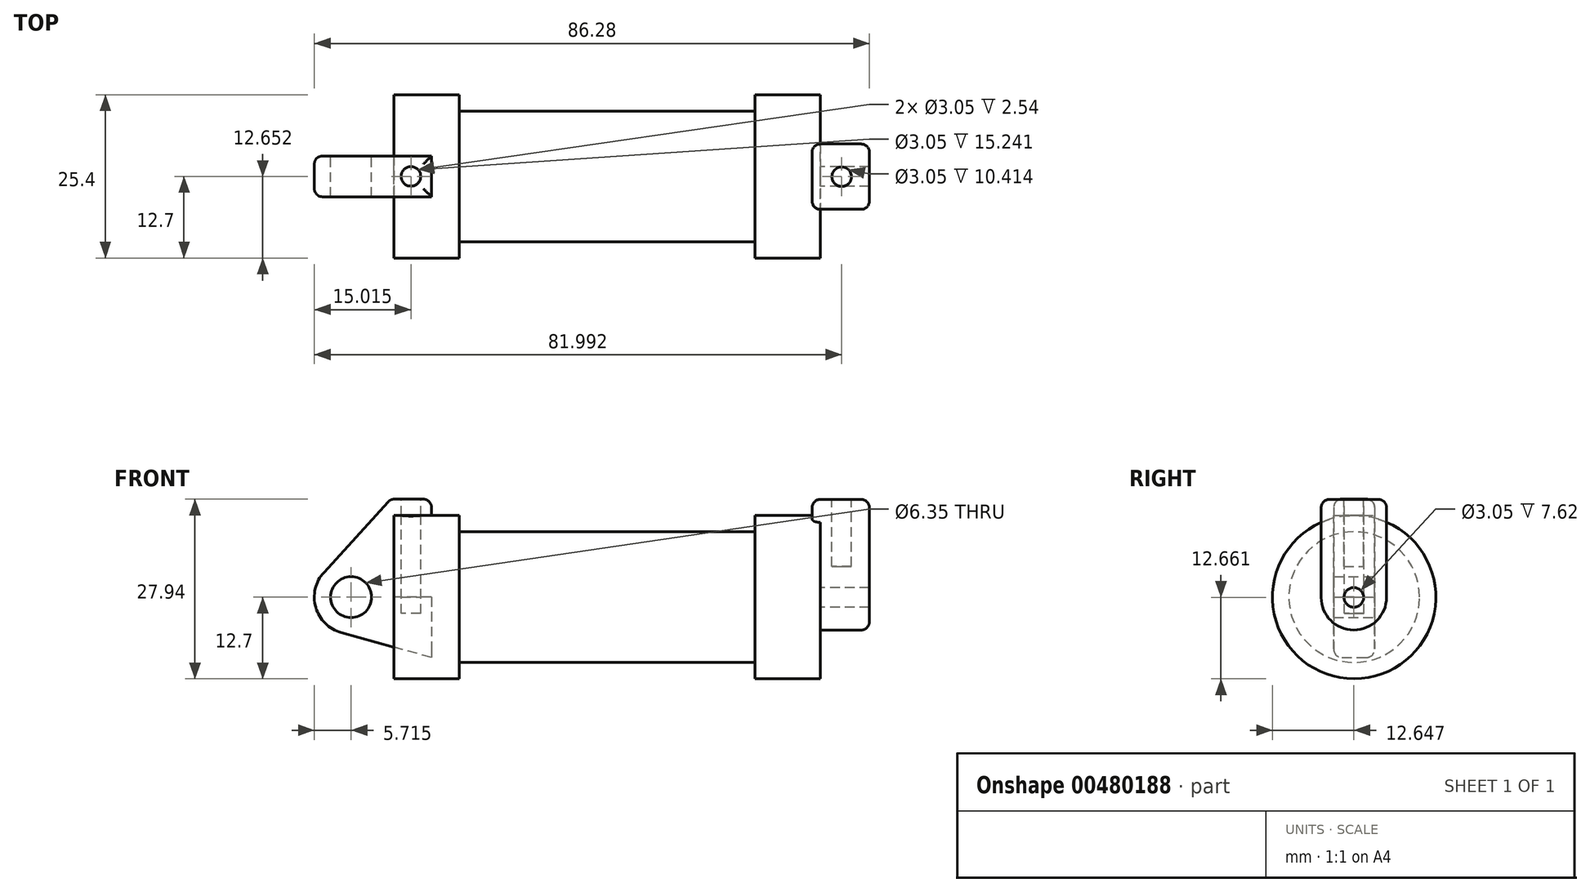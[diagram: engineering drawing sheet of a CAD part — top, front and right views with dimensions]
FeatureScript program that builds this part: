
annotation { "Feature Type Name" : "Feature", "Feature Type Description" : "" }
export const myFeature = defineFeature(function(context is Context, id is Id, definition is map)
    precondition{}
    {
        {
            var Q0;
            Q0=qCreatedBy(makeId("Front.planeOp"),FACE);
            var sketch = newSketch(context, id + "F0", { "sketchPlane" : qUnion([Q0])});
            skLineSegment(sketch, "E0", {"start": v(0, 0) * mm, "end": v(0, 12.7) * mm});
            skLineSegment(sketch, "E1", {"start": v(0, 12.7) * mm, "end": v(10.16, 12.7) * mm});
            skLineSegment(sketch, "E2", {"start": v(10.16, 12.7) * mm, "end": v(10.16, 10.16) * mm});
            skLineSegment(sketch, "E3", {"start": v(10.16, 10.16) * mm, "end": v(56.13, 10.16) * mm});
            skLineSegment(sketch, "E4", {"start": v(56.13, 10.16) * mm, "end": v(56.13, 12.7) * mm});
            skLineSegment(sketch, "E5", {"start": v(56.13, 12.7) * mm, "end": v(66.3, 12.7) * mm});
            skLineSegment(sketch, "E6", {"start": v(66.3, 12.7) * mm, "end": v(66.3, 0) * mm});
            skLineSegment(sketch, "E7", {"start": v(66.3, 0) * mm, "end": v(0, 0) * mm});
            skLineSegment(sketch, "E8", {"start": v(5.84, 15.24) * mm, "end": v(-0.5, 15.24) * mm});
            skLineSegment(sketch, "E9", {"start": v(-0.5, 15.24) * mm, "end": v(-10.88, 3.85) * mm});
            skLineSegment(sketch, "E10", {"start": v(0, 0) * mm, "end": v(-6.65, 0) * mm});
            skCircle(sketch, "E11", {"center": v(-6.65, 0) * mm, "radius": 5.72 * mm});
            skCircle(sketch, "E12", {"center": v(-6.65, 0) * mm, "radius": 3.18 * mm});
            skLineSegment(sketch, "E13", {"start": v(5.84, 15.24) * mm, "end": v(5.84, -9.4) * mm});
            skLineSegment(sketch, "E14", {"start": v(5.84, -9.4) * mm, "end": v(-8.18, -5.5) * mm});
            skSolve(sketch);
        }
        {
            var Q0;
            {var subQ0=sQuery(id+"F0.wireOp",EDGE,"E2");Q0=makeQuery(id+"F0.imprint","IMPRINT",FACE,{"disambiguationData":[TD([[makeQuery(id+"F0.imprint","IMPRINT",EDGE,{"derivedFrom":subQ0}),-1.0]])]});}
            var Q1;
            {var subQ0=sQuery(id+"F0.wireOp",EDGE,"E0");Q1=makeQuery(id+"F0.imprint","IMPRINT",FACE,{"disambiguationData":[TD([[makeQuery(id+"F0.imprint","IMPRINT",EDGE,{"derivedFrom":subQ0}),-1.0]])]});}
            var Q2;
            Q2=sQuery(id+"F0.wireOp",EDGE,"E7");
            revolve(context, id + "F1", {"entities" : qUnion([Q0, Q1]), "axis" : qUnion([Q2]), "revolveType" : RevolveType.FULL});
        }
        {
            var Q0;
            Q0=makeQuery(id+"F1.opRevolve","SWEPT_FACE",FACE,{"disambiguationData":[OSD([sQuery(id+"F0.wireOp",EDGE,"E6")])]});
            var sketch = newSketch(context, id + "F2", { "sketchPlane" : qUnion([Q0])});
            skSolve(sketch);
        }
        {
            var Q0;
            {var subQ1=sQuery(id+"F0.wireOp",EDGE,"E0");Q0=makeQuery(id+"F0.imprint","IMPRINT",FACE,{"disambiguationData":[TD([[makeQuery(id+"F0.imprint","IMPRINT",EDGE,{"derivedFrom":subQ1}),1.0]])]});}
            var Q1;
            {var subQ0=sQuery(id+"F0.wireOp",EDGE,"E14");Q1=makeQuery(id+"F0.imprint","IMPRINT",FACE,{"disambiguationData":[TD([[makeQuery(id+"F0.imprint","IMPRINT",EDGE,{"derivedFrom":subQ0}),-1.0]])]});}
            var Q2;
            {var subQ5=sQuery(id+"F0.wireOp",EDGE,"E12");Q2=makeQuery(id+"F0.imprint","IMPRINT",FACE,{"disambiguationData":[TD([[makeQuery(id+"F0.imprint","IMPRINT",EDGE,{"derivedFrom":subQ5}),-1.0]])]});}
            extrude(context, id + "F3", {"entities" : qUnion([Q0, Q1, Q2]), "endBound" : BoundingType.SYMMETRIC, "depth" : 6.35 * mm});
        }
        {
            var Q0;
            Q0=makeQuery(id+"F2.imprint","IMPRINT",FACE,{"disambiguationData":[TD([[makeQuery(id+"F2.imprint","IMPRINT",EDGE,{"derivedFrom":makeQuery(id+"F1.opRevolve","SWEPT_EDGE",EDGE,{"disambiguationData":[OSD([sQuery(id+"F0.wireOp",EDGE,"E5"),sQuery(id+"F0.wireOp",EDGE,"E6")])]})}),1.0]])]});
            var sketch = newSketch(context, id + "F4", { "sketchPlane" : qUnion([Q0])});
            skCircle(sketch, "E15", {"center": v(-0.05, -0.04) * mm, "radius": 5.08 * mm});
            skLineSegment(sketch, "E16", {"start": v(5.03, -0.04) * mm, "end": v(5.03, 15.2) * mm});
            skLineSegment(sketch, "E17", {"start": v(-5.13, -0.04) * mm, "end": v(-5.13, 15.2) * mm});
            skCircle(sketch, "E18", {"center": v(-0.05, -0.04) * mm, "radius": 1.52 * mm});
            skLineSegment(sketch, "E19", {"start": v(-5.13, 15.2) * mm, "end": v(5.03, 15.2) * mm});
            skSolve(sketch);
        }
        {
            var Q0;
            Q0 = qSketchRegion(id + "F4", true);
            extrude(context, id + "F5", {"entities" : qUnion([Q0]), "operationType" : NewBodyOperationType.ADD, "depth" : 7.62 * mm, "hasSecondDirection" : true, "secondDirectionOppositeDirection" : true, "secondDirectionDepth" : 1.27 * mm});
        }
        {
            var Q0;
            Q0=makeQuery(id+"F3.opExtrude","SWEPT_FACE",FACE,{"disambiguationData":[OSD([sQuery(id+"F0.wireOp",EDGE,"E8")])]});
            var sketch = newSketch(context, id + "F6", { "sketchPlane" : qUnion([Q0])});
            skCircle(sketch, "E20", {"center": v(2.64, 0) * mm, "radius": 1.52 * mm});
            skSolve(sketch);
        }
        {
            var Q0;
            Q0=makeQuery(id+"F6.imprint","IMPRINT",FACE,{"disambiguationData":[TD([[makeQuery(id+"F6.imprint","IMPRINT",EDGE,{"derivedFrom":sQuery(id+"F6.wireOp",EDGE,"E20")}),1.0]])]});
            extrude(context, id + "F7", {"entities" : qUnion([Q0]), "operationType" : NewBodyOperationType.REMOVE, "oppositeDirection" : true, "depth" : 17.78 * mm});
        }
        {
            var Q0;
            Q0=makeQuery(id+"F5.opExtrude","SWEPT_FACE",FACE,{"disambiguationData":[OSD([sQuery(id+"F4.wireOp",EDGE,"E19")])]});
            var sketch = newSketch(context, id + "F8", { "sketchPlane" : qUnion([Q0])});
            skCircle(sketch, "E21", {"center": v(69.62, -0.04) * mm, "radius": 1.52 * mm});
            skPoint(sketch, "E21.centerSnap0", {"position": v(65.02, -0.04) * mm});
            skSolve(sketch);
        }
        {
            var Q0;
            Q0=makeQuery(id+"F8.imprint","IMPRINT",FACE,{"disambiguationData":[TD([[makeQuery(id+"F8.imprint","IMPRINT",EDGE,{"derivedFrom":sQuery(id+"F8.wireOp",EDGE,"E21")}),1.0]])]});
            extrude(context, id + "F9", {"entities" : qUnion([Q0]), "operationType" : NewBodyOperationType.REMOVE, "oppositeDirection" : true, "depth" : 10.4 * mm});
        }
        {
            var Q0;
            Q0=makeQuery(id+"F5.opExtrude","SWEPT_EDGE",EDGE,{"disambiguationData":[OSD([sQuery(id+"F4.wireOp",EDGE,"E16"),sQuery(id+"F4.wireOp",EDGE,"E19")])]});
            var Q1;
            Q1=makeQuery(id+"F5.opExtrude","CAP_EDGE",EDGE,{"disambiguationData":[OSD([sQuery(id+"F4.wireOp",EDGE,"E19")])],"isStart":true});
            var Q2;
            Q2=makeQuery(id+"F5.opExtrude","SWEPT_EDGE",EDGE,{"disambiguationData":[OSD([sQuery(id+"F4.wireOp",EDGE,"E17"),sQuery(id+"F4.wireOp",EDGE,"E19")])]});
            var Q3;
            Q3=makeQuery(id+"F5.opExtrude","CAP_EDGE",EDGE,{"disambiguationData":[OSD([sQuery(id+"F4.wireOp",EDGE,"E19")])],"isStart":false});
            var Q4;
            Q4=makeQuery(id+"F3.opExtrude","CAP_EDGE",EDGE,{"disambiguationData":[OSD([sQuery(id+"F0.wireOp",EDGE,"E8")])],"isStart":true});
            var Q5;
            Q5=makeQuery(id+"F3.opExtrude","SWEPT_EDGE",EDGE,{"disambiguationData":[OSD([sQuery(id+"F0.wireOp",EDGE,"E8"),sQuery(id+"F0.wireOp",EDGE,"E9")])]});
            var Q6;
            Q6=makeQuery(id+"F3.opExtrude","CAP_EDGE",EDGE,{"disambiguationData":[OSD([sQuery(id+"F0.wireOp",EDGE,"E8")])],"isStart":false});
            var Q7;
            Q7=makeQuery(id+"F3.opExtrude","SWEPT_EDGE",EDGE,{"disambiguationData":[OSD([sQuery(id+"F0.wireOp",EDGE,"E8"),sQuery(id+"F0.wireOp",EDGE,"E13")])]});
            var Q8;
            Q8=makeQuery(id+"F5.opExtrude","CAP_EDGE",EDGE,{"disambiguationData":[OSD([sQuery(id+"F4.wireOp",EDGE,"E16")])],"isStart":true});
            var Q9;
            Q9=makeQuery(id+"F5.opExtrude","CAP_EDGE",EDGE,{"disambiguationData":[OSD([sQuery(id+"F4.wireOp",EDGE,"E17")])],"isStart":true});
            var Q10;
            Q10=makeQuery(id+"F5.opExtrude","CAP_EDGE",EDGE,{"disambiguationData":[OSD([sQuery(id+"F4.wireOp",EDGE,"E16")])],"isStart":false});
            var Q11;
            Q11=makeQuery(id+"F5.opExtrude","CAP_EDGE",EDGE,{"disambiguationData":[OSD([sQuery(id+"F4.wireOp",EDGE,"E15")])],"isStart":false});
            var Q12;
            Q12=makeQuery(id+"F3.opExtrude","CAP_EDGE",EDGE,{"disambiguationData":[OSD([sQuery(id+"F0.wireOp",EDGE,"E9")])],"isStart":true});
            var Q13;
            Q13=makeQuery(id+"F3.opExtrude","CAP_EDGE",EDGE,{"disambiguationData":[OSD([sQuery(id+"F0.wireOp",EDGE,"E9")])],"isStart":false});
            var Q14;
            Q14=makeQuery(id+"F3.opExtrude","CAP_EDGE",EDGE,{"disambiguationData":[OSD([sQuery(id+"F0.wireOp",EDGE,"E11")])],"isStart":true});
            var Q15;
            Q15=makeQuery(id+"F3.opExtrude","CAP_EDGE",EDGE,{"disambiguationData":[OSD([sQuery(id+"F0.wireOp",EDGE,"E11")])],"isStart":false});
            var Q16;
            Q16=makeQuery(id+"F3.opExtrude","CAP_EDGE",EDGE,{"disambiguationData":[OSD([sQuery(id+"F0.wireOp",EDGE,"E14")])],"isStart":true});
            var Q17;
            Q17=makeQuery(id+"F3.opExtrude","CAP_EDGE",EDGE,{"disambiguationData":[OSD([sQuery(id+"F0.wireOp",EDGE,"E14")])],"isStart":false});
            var Q18;
            Q18=makeQuery(id+"F5.opExtrude","CAP_EDGE",EDGE,{"disambiguationData":[OSD([sQuery(id+"F4.wireOp",EDGE,"E17")])],"isStart":false});
            fillet(context, id + "F10", {"entities" : qUnion([Q0, Q1, Q2, Q3, Q4, Q5, Q6, Q7, Q8, Q9, Q10, Q11, Q12, Q13, Q14, Q15, Q16, Q17, Q18]), "radius" : 1.27 * mm, "tangentPropagation" : true, "allowEdgeOverflow" : false});
        }
    });
